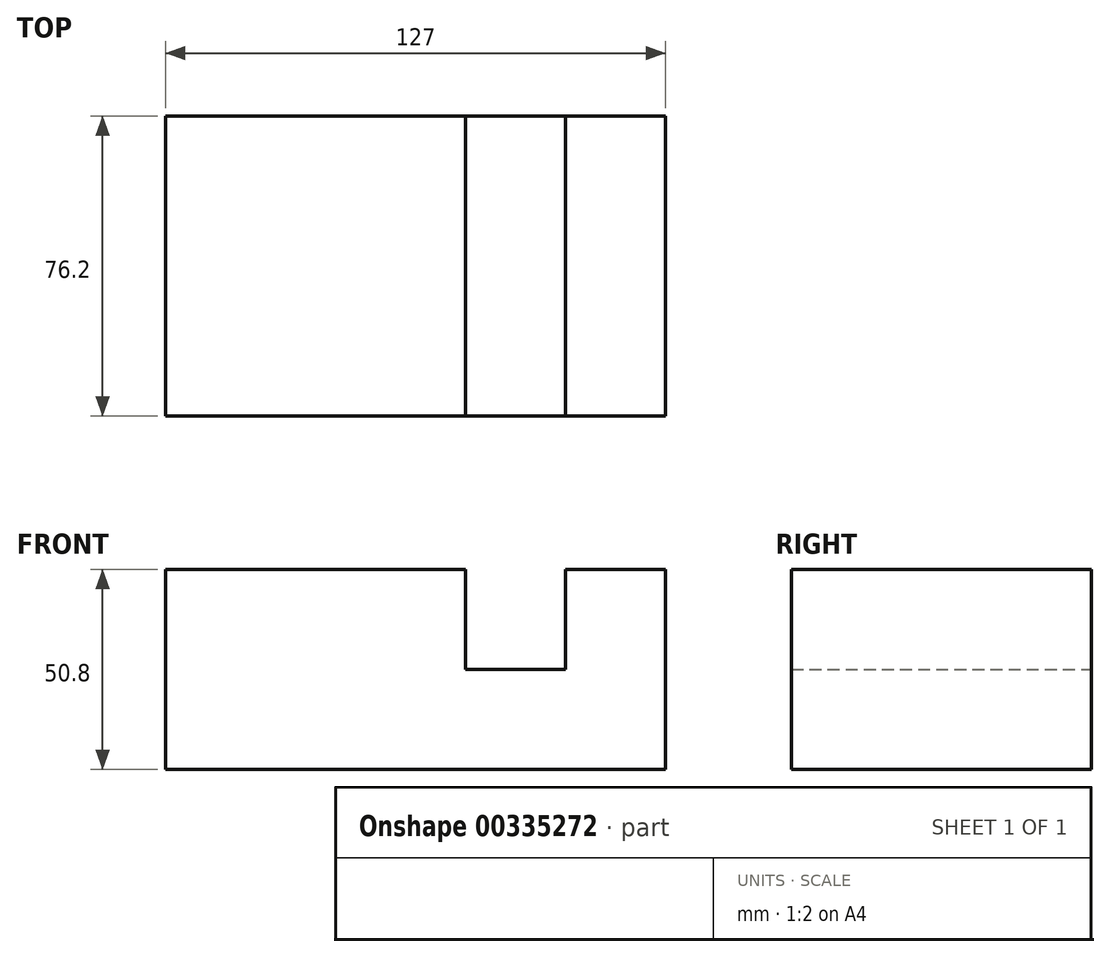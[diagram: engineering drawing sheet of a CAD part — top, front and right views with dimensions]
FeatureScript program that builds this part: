
annotation { "Feature Type Name" : "Feature", "Feature Type Description" : "" }
export const myFeature = defineFeature(function(context is Context, id is Id, definition is map)
    precondition{}
    {
        {
            var Q0;
            Q0=qCreatedBy(makeId("Front.planeOp"),FACE);
            var sketch = newSketch(context, id + "F0", { "sketchPlane" : qUnion([Q0])});
            skLineSegment(sketch, "E0", {"start": v(0, 0) * mm, "end": v(0, 50.8) * mm});
            skLineSegment(sketch, "E1", {"start": v(0, 50.8) * mm, "end": v(76.2, 50.8) * mm});
            skLineSegment(sketch, "E2", {"start": v(76.2, 50.8) * mm, "end": v(76.2, 25.4) * mm});
            skLineSegment(sketch, "E3", {"start": v(76.2, 25.4) * mm, "end": v(101.6, 25.4) * mm});
            skLineSegment(sketch, "E4", {"start": v(101.6, 25.4) * mm, "end": v(101.6, 50.8) * mm});
            skLineSegment(sketch, "E5", {"start": v(101.6, 50.8) * mm, "end": v(127, 50.8) * mm});
            skLineSegment(sketch, "E6", {"start": v(127, 50.8) * mm, "end": v(127, 0) * mm});
            skLineSegment(sketch, "E7", {"start": v(127, 0) * mm, "end": v(0, 0) * mm});
            skSolve(sketch);
        }
        {
            var Q0;
            Q0 = qSketchRegion(id + "F0", true);
            extrude(context, id + "F1", {"entities" : qUnion([Q0]), "depth" : 76.2 * mm});
        }
    });
